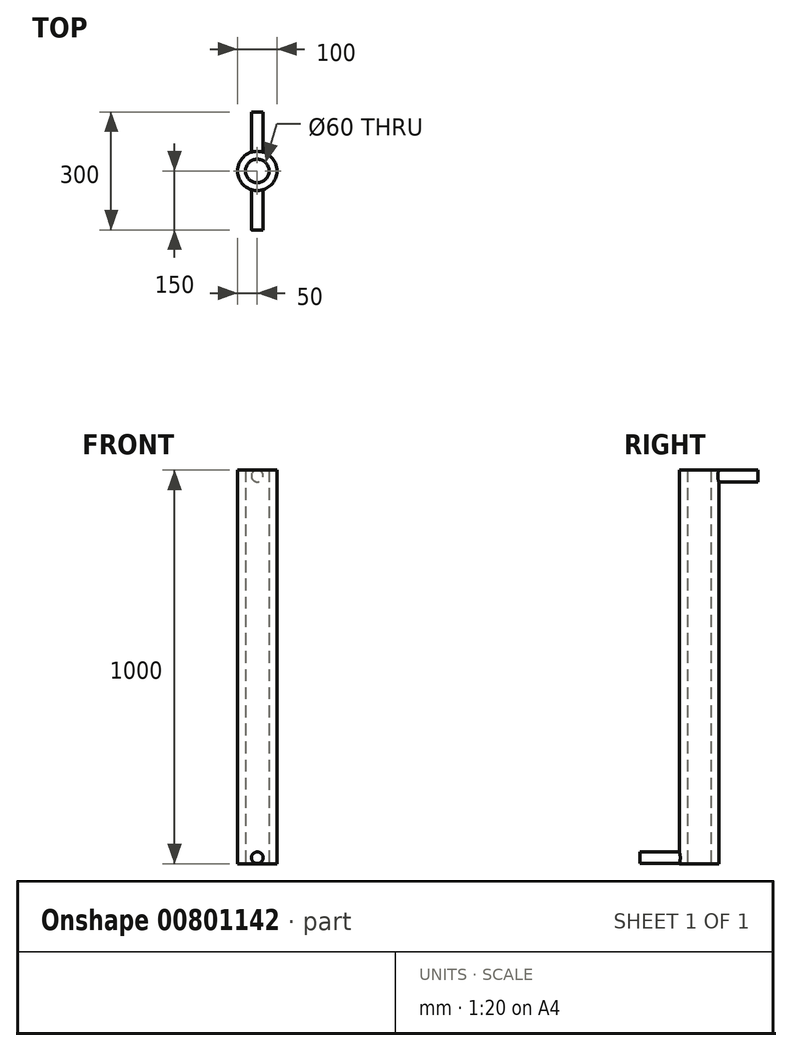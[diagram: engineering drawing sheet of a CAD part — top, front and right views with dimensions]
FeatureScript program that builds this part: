
annotation { "Feature Type Name" : "Feature", "Feature Type Description" : "" }
export const myFeature = defineFeature(function(context is Context, id is Id, definition is map)
    precondition{}
    {
        {
            var Q0;
            Q0=qCreatedBy(makeId("Top.planeOp"),FACE);
            var sketch = newSketch(context, id + "F0", { "sketchPlane" : qUnion([Q0])});
            skCircle(sketch, "E0", {"center": v(0, 0) * mm, "radius": 50 * mm});
            skCircle(sketch, "E1", {"center": v(0, 0) * mm, "radius": 30 * mm});
            skSolve(sketch);
        }
        {
            var Q0;
            Q0 = qSketchRegion(id + "F0", true);
            extrude(context, id + "F1", {"entities" : qUnion([Q0]), "depth" : 1000 * mm, "offsetDistance" : 25 * mm});
        }
        {
            var Q0;
            Q0=qCreatedBy(makeId("Front.planeOp"),FACE);
            cPlane(context, id + "F2", {"entities" : qUnion([Q0]), "cplaneType" : CPlaneType.OFFSET, "offset" : 50 * mm, "width" : 150 * mm, "height" : 150 * mm});
        }
        {
            var Q0;
            Q0=qCreatedBy(id+"F2.planeOp",FACE);
            var sketch = newSketch(context, id + "F3", { "sketchPlane" : qUnion([Q0])});
            skCircle(sketch, "E2", {"center": v(0, 15) * mm, "radius": 14.76 * mm});
            skSolve(sketch);
        }
        {
            var Q0;
            Q0=makeQuery(id+"F3.imprint","IMPRINT",FACE,{"disambiguationData":[TD([[makeQuery(id+"F3.imprint","IMPRINT",EDGE,{"derivedFrom":sQuery(id+"F3.wireOp",EDGE,"E2")}),1.0]])]});
            var Q1;
            Q1=sQuery(id+"F3.wireOp",EDGE,"E2");
            extrude(context, id + "F4", {"entities" : qUnion([Q0]), "operationType" : NewBodyOperationType.ADD, "surfaceOperationType" : NewSurfaceOperationType.ADD, "surfaceEntities" : qUnion([Q1]), "depth" : 100 * mm, "offsetDistance" : 25 * mm, "hasSecondDirection" : true, "secondDirectionOppositeDirection" : true, "secondDirectionDepth" : 7 * mm});
        }
        {
            var Q0;
            Q0=qCreatedBy(makeId("Front.planeOp"),FACE);
            cPlane(context, id + "F5", {"entities" : qUnion([Q0]), "cplaneType" : CPlaneType.OFFSET, "offset" : 50 * mm, "oppositeDirection" : true, "width" : 150 * mm, "height" : 150 * mm});
        }
        {
            var Q0;
            Q0=qCreatedBy(id+"F5.planeOp",FACE);
            var sketch = newSketch(context, id + "F6", { "sketchPlane" : qUnion([Q0])});
            skCircle(sketch, "E3", {"center": v(0, 985) * mm, "radius": 15 * mm});
            skSolve(sketch);
        }
        {
            var Q0;
            Q0 = qSketchRegion(id + "F6", true);
            extrude(context, id + "F7", {"entities" : qUnion([Q0]), "operationType" : NewBodyOperationType.ADD, "oppositeDirection" : true, "depth" : 100 * mm, "offsetDistance" : 25 * mm, "hasSecondDirection" : true, "secondDirectionOppositeDirection" : false, "secondDirectionDepth" : 7 * mm});
        }
    });
